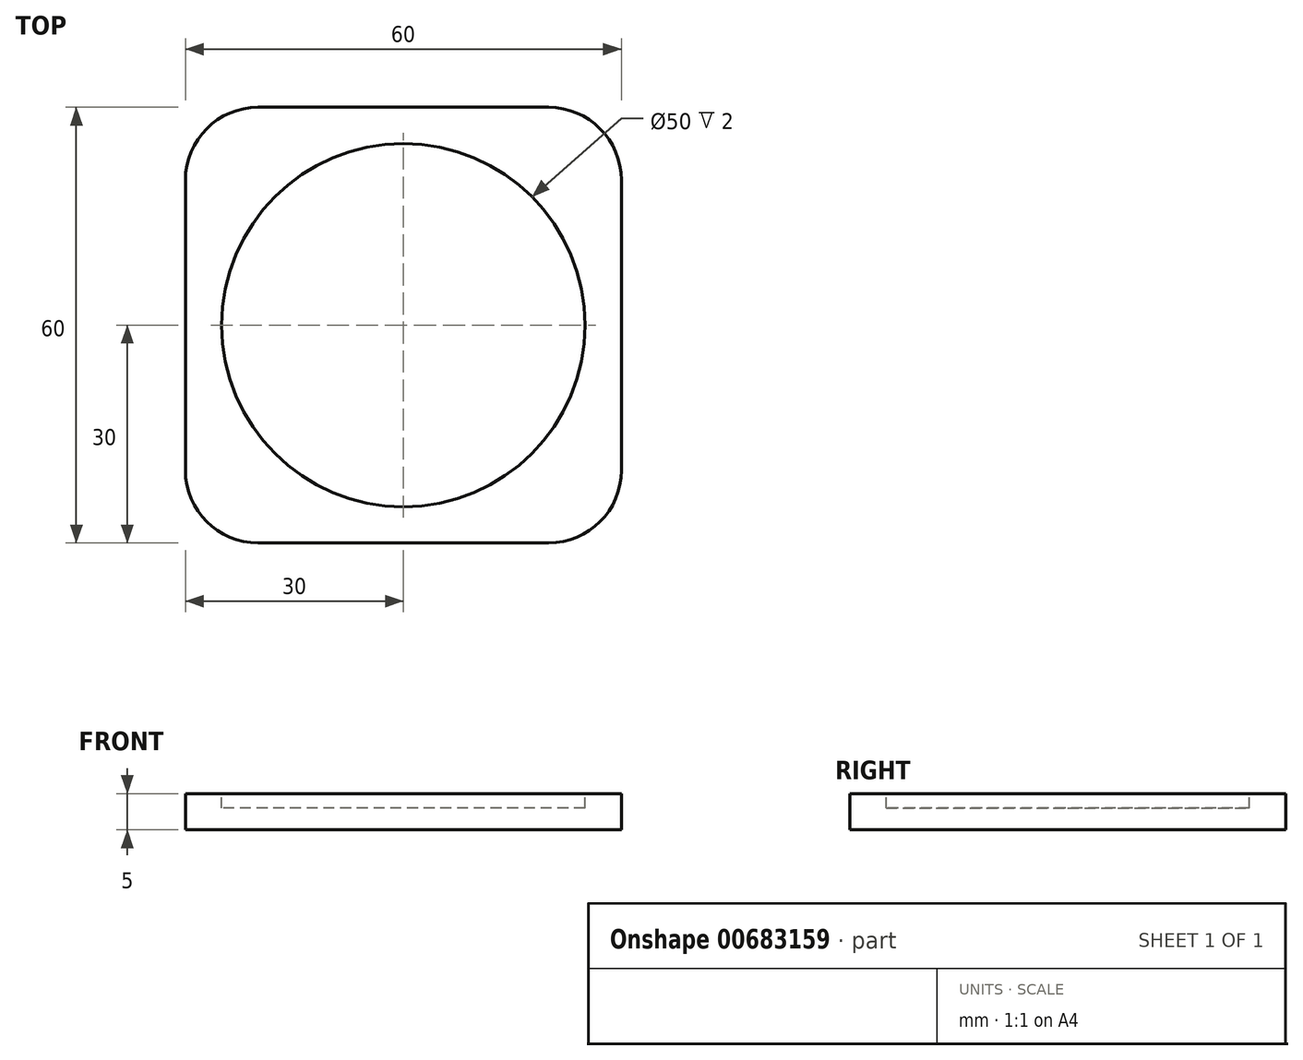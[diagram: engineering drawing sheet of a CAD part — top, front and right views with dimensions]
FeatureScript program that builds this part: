
annotation { "Feature Type Name" : "Feature", "Feature Type Description" : "" }
export const myFeature = defineFeature(function(context is Context, id is Id, definition is map)
    precondition{}
    {
        {
            var Q0;
            Q0=qCreatedBy(makeId("Top.planeOp"),FACE);
            var sketch = newSketch(context, id + "F0", { "sketchPlane" : qUnion([Q0])});
            skLineSegment(sketch, "E0.bottom", {"start": v(-30, 30) * mm, "end": v(30, 30) * mm});
            skLineSegment(sketch, "E0.top", {"start": v(-30, -30) * mm, "end": v(30, -30) * mm});
            skLineSegment(sketch, "E0.left", {"start": v(-30, 30) * mm, "end": v(-30, -30) * mm});
            skLineSegment(sketch, "E0.right", {"start": v(30, 30) * mm, "end": v(30, -30) * mm});
            skSolve(sketch);
        }
        {
            var Q0;
            Q0=makeQuery(id+"F0.imprint","IMPRINT",FACE,{"disambiguationData":[TD([[makeQuery(id+"F0.imprint","IMPRINT",EDGE,{"derivedFrom":sQuery(id+"F0.wireOp",EDGE,"E0.bottom")}),-1.0]])]});
            extrude(context, id + "F1", {"entities" : qUnion([Q0]), "depth" : 5 * mm, "offsetDistance" : 25 * mm});
        }
        {
            var Q0;
            Q0=makeQuery(id+"F1.opExtrude","SWEPT_EDGE",EDGE,{"disambiguationData":[OSD([sQuery(id+"F0.wireOp",EDGE,"E0.top"),sQuery(id+"F0.wireOp",EDGE,"E0.right")])]});
            var Q1;
            Q1=makeQuery(id+"F1.opExtrude","SWEPT_EDGE",EDGE,{"disambiguationData":[OSD([sQuery(id+"F0.wireOp",EDGE,"E0.bottom"),sQuery(id+"F0.wireOp",EDGE,"E0.right")])]});
            var Q2;
            Q2=makeQuery(id+"F1.opExtrude","SWEPT_EDGE",EDGE,{"disambiguationData":[OSD([sQuery(id+"F0.wireOp",EDGE,"E0.top"),sQuery(id+"F0.wireOp",EDGE,"E0.left")])]});
            var Q3;
            Q3=makeQuery(id+"F1.opExtrude","SWEPT_EDGE",EDGE,{"disambiguationData":[OSD([sQuery(id+"F0.wireOp",EDGE,"E0.bottom"),sQuery(id+"F0.wireOp",EDGE,"E0.left")])]});
            fillet(context, id + "F2", {"entities" : qUnion([Q0, Q1, Q2, Q3]), "radius" : 10 * mm, "tangentPropagation" : true, "allowEdgeOverflow" : false});
        }
        {
            var Q0;
            Q0=makeQuery(id+"F1.opExtrude","CAP_FACE",FACE,{"disambiguationData":[OSD([sQuery(id+"F0.wireOp",EDGE,"E0.bottom"),sQuery(id+"F0.wireOp",EDGE,"E0.top"),sQuery(id+"F0.wireOp",EDGE,"E0.left"),sQuery(id+"F0.wireOp",EDGE,"E0.right")])],"isStart":false});
            var sketch = newSketch(context, id + "F3", { "sketchPlane" : qUnion([Q0])});
            skCircle(sketch, "E1", {"center": v(0, 0) * mm, "radius": 25 * mm});
            skSolve(sketch);
        }
        {
            var Q0;
            Q0=makeQuery(id+"F3.imprint","IMPRINT",FACE,{"disambiguationData":[TD([[makeQuery(id+"F3.imprint","IMPRINT",EDGE,{"derivedFrom":sQuery(id+"F3.wireOp",EDGE,"E1")}),1.0]])]});
            extrude(context, id + "F4", {"entities" : qUnion([Q0]), "operationType" : NewBodyOperationType.REMOVE, "oppositeDirection" : true, "depth" : 2 * mm, "offsetDistance" : 25 * mm});
        }
    });
